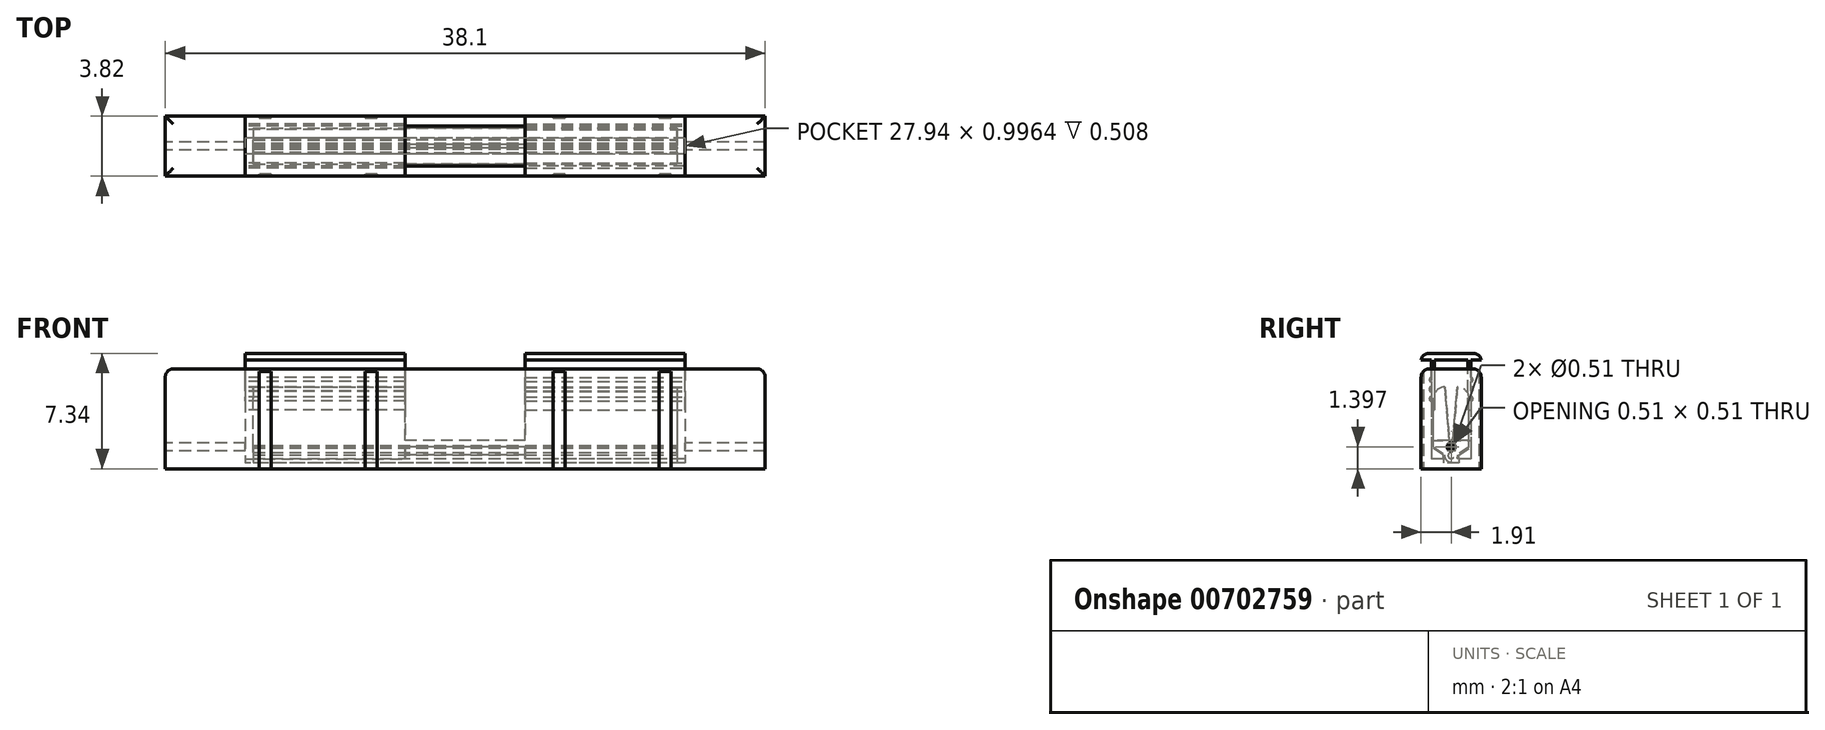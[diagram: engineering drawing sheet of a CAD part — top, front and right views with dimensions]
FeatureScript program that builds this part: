
annotation { "Feature Type Name" : "Feature", "Feature Type Description" : "" }
export const myFeature = defineFeature(function(context is Context, id is Id, definition is map)
    precondition{}
    {
        {
            var Q0;
            Q0=qCreatedBy(makeId("Top.planeOp"),FACE);
            var sketch = newSketch(context, id + "F0", { "sketchPlane" : qUnion([Q0])});
            skLineSegment(sketch, "E0.bottom", {"start": v(19.05, -1.9) * mm, "end": v(-19.05, -1.9) * mm});
            skLineSegment(sketch, "E0.top", {"start": v(19.05, 1.9) * mm, "end": v(-19.05, 1.9) * mm});
            skLineSegment(sketch, "E0.left", {"start": v(19.05, -1.9) * mm, "end": v(19.05, 1.9) * mm});
            skLineSegment(sketch, "E0.right", {"start": v(-19.05, -1.9) * mm, "end": v(-19.05, 1.9) * mm});
            skPoint(sketch, "E0.middle", {"position": v(0, 0) * mm});
            skLineSegment(sketch, "E1", {"start": v(0, 6.77) * mm, "end": v(0, -8.48) * mm, "construction": true});
            skLineSegment(sketch, "E2.bottom", {"start": v(-13.97, 1.27) * mm, "end": v(-3.81, 1.27) * mm});
            skLineSegment(sketch, "E2.top", {"start": v(-13.97, -1.27) * mm, "end": v(-3.81, -1.27) * mm});
            skLineSegment(sketch, "E2.left", {"start": v(-13.97, 1.27) * mm, "end": v(-13.97, -1.27) * mm});
            skLineSegment(sketch, "E2.right", {"start": v(-3.81, 1.27) * mm, "end": v(-3.81, -1.27) * mm});
            skLineSegment(sketch, "E3.MirrorCS", {"start": v(3.81, 1.27) * mm, "end": v(3.81, -1.27) * mm});
            skLineSegment(sketch, "E4.MirrorCS", {"start": v(13.97, 1.27) * mm, "end": v(3.81, 1.27) * mm});
            skLineSegment(sketch, "E5.MirrorCS", {"start": v(13.97, -1.27) * mm, "end": v(3.81, -1.27) * mm});
            skLineSegment(sketch, "E6.MirrorCS", {"start": v(13.97, 1.27) * mm, "end": v(13.97, -1.27) * mm});
            skLineSegment(sketch, "E7", {"start": v(13.08, 1.9) * mm, "end": v(13.08, 1.78) * mm});
            skLineSegment(sketch, "E8", {"start": v(13.08, 1.78) * mm, "end": v(12.32, 1.78) * mm});
            skLineSegment(sketch, "E9", {"start": v(12.32, 1.78) * mm, "end": v(12.32, 1.9) * mm});
            skLineSegment(sketch, "E10", {"start": v(26.93, 0) * mm, "end": v(-31.8, 0) * mm, "construction": true});
            skPoint(sketch, "E10.startSnap0", {"position": v(19.05, 0) * mm});
            skLineSegment(sketch, "E11", {"start": v(6.35, 1.9) * mm, "end": v(6.35, 1.78) * mm});
            skLineSegment(sketch, "E12", {"start": v(6.35, 1.78) * mm, "end": v(5.59, 1.78) * mm});
            skLineSegment(sketch, "E13", {"start": v(5.59, 1.78) * mm, "end": v(5.59, 1.9) * mm});
            skLineSegment(sketch, "E14.MirrorCS", {"start": v(6.35, -1.9) * mm, "end": v(6.35, -1.78) * mm});
            skLineSegment(sketch, "E15.MirrorCS", {"start": v(6.35, -1.78) * mm, "end": v(5.59, -1.78) * mm});
            skLineSegment(sketch, "E16.MirrorCS", {"start": v(5.59, -1.78) * mm, "end": v(5.59, -1.9) * mm});
            skLineSegment(sketch, "E17.MirrorCS", {"start": v(12.32, -1.78) * mm, "end": v(12.32, -1.9) * mm});
            skLineSegment(sketch, "E18.MirrorCS", {"start": v(13.08, -1.78) * mm, "end": v(12.32, -1.78) * mm});
            skLineSegment(sketch, "E19.MirrorCS", {"start": v(13.08, -1.9) * mm, "end": v(13.08, -1.78) * mm});
            skLineSegment(sketch, "E20.MirrorCS", {"start": v(-6.35, 1.78) * mm, "end": v(-5.59, 1.78) * mm});
            skLineSegment(sketch, "E21.MirrorCS", {"start": v(-5.59, 1.78) * mm, "end": v(-5.59, 1.9) * mm});
            skLineSegment(sketch, "E22.MirrorCS", {"start": v(-6.35, 1.9) * mm, "end": v(-6.35, 1.78) * mm});
            skLineSegment(sketch, "E23.MirrorCS", {"start": v(-12.32, 1.78) * mm, "end": v(-12.32, 1.9) * mm});
            skLineSegment(sketch, "E24.MirrorCS", {"start": v(-13.08, 1.78) * mm, "end": v(-12.32, 1.78) * mm});
            skLineSegment(sketch, "E25.MirrorCS", {"start": v(-13.08, 1.9) * mm, "end": v(-13.08, 1.78) * mm});
            skLineSegment(sketch, "E26.MirrorCS", {"start": v(-6.35, -1.9) * mm, "end": v(-6.35, -1.78) * mm});
            skLineSegment(sketch, "E27.MirrorCS", {"start": v(-6.35, -1.78) * mm, "end": v(-5.59, -1.78) * mm});
            skLineSegment(sketch, "E28.MirrorCS", {"start": v(-5.59, -1.78) * mm, "end": v(-5.59, -1.9) * mm});
            skLineSegment(sketch, "E29.MirrorCS", {"start": v(-13.08, -1.9) * mm, "end": v(-13.08, -1.78) * mm});
            skLineSegment(sketch, "E30.MirrorCS", {"start": v(-13.08, -1.78) * mm, "end": v(-12.32, -1.78) * mm});
            skLineSegment(sketch, "E31.MirrorCS", {"start": v(-12.32, -1.78) * mm, "end": v(-12.32, -1.9) * mm});
            skSolve(sketch);
        }
        {
            var Q0;
            Q0=makeQuery(id+"F0.imprint","IMPRINT",FACE,{"disambiguationData":[TD([[makeQuery(id+"F0.imprint","IMPRINT",EDGE,{"derivedFrom":sQuery(id+"F0.wireOp",EDGE,"E0.top")}),1.0]])]});
            extrude(context, id + "F1", {"entities" : qUnion([Q0]), "depth" : 6.35 * mm, "offsetDistance" : 25.4 * mm});
        }
        {
            var Q0;
            Q0=makeQuery(id+"F0.imprint","IMPRINT",FACE,{"disambiguationData":[TD([[makeQuery(id+"F0.imprint","IMPRINT",EDGE,{"derivedFrom":sQuery(id+"F0.wireOp",EDGE,"E2.bottom")}),-1.0]])]});
            var Q1;
            Q1=makeQuery(id+"F0.imprint","IMPRINT",FACE,{"disambiguationData":[TD([[makeQuery(id+"F0.imprint","IMPRINT",EDGE,{"derivedFrom":sQuery(id+"F0.wireOp",EDGE,"E3.MirrorCS")}),1.0]])]});
            extrude(context, id + "F2", {"entities" : qUnion([Q0, Q1]), "operationType" : NewBodyOperationType.ADD, "depth" : 0.64 * mm, "offsetDistance" : 25.4 * mm});
        }
        {
            var Q0;
            Q0=makeQuery(id+"F1.opExtrude","SWEPT_FACE",FACE,{"disambiguationData":[OSD([sQuery(id+"F0.wireOp",EDGE,"E2.left")])]});
            var sketch = newSketch(context, id + "F3", { "sketchPlane" : qUnion([Q0])});
            skLineSegment(sketch, "E32.bottom", {"start": v(0.5, 0.38) * mm, "end": v(-0.5, 0.38) * mm});
            skLineSegment(sketch, "E32.top", {"start": v(1.27, 5.46) * mm, "end": v(-1.27, 5.46) * mm});
            skLineSegment(sketch, "E32.left", {"start": v(1.27, 1.4) * mm, "end": v(1.27, 5.46) * mm});
            skLineSegment(sketch, "E32.right", {"start": v(-1.27, 1.4) * mm, "end": v(-1.27, 5.46) * mm});
            skLineSegment(sketch, "E33", {"start": v(0, 0) * mm, "end": v(0, 8.58) * mm, "construction": true});
            skPoint(sketch, "E34", {"position": v(0, 0.99) * mm});
            skLineSegment(sketch, "E35", {"start": v(0.5, 0.89) * mm, "end": v(0.5, 0.38) * mm});
            skLineSegment(sketch, "E36.MirrorCS", {"start": v(-0.5, 0.89) * mm, "end": v(-0.5, 0.38) * mm});
            skPoint(sketch, "E37.orphan", {"position": v(-0.5, 0.38) * mm});
            skPoint(sketch, "E38.orphan", {"position": v(1.27, 0.38) * mm});
            skLineSegment(sketch, "E39", {"start": v(1.27, 1.4) * mm, "end": v(0.5, 0.89) * mm});
            skLineSegment(sketch, "E40.MirrorCS", {"start": v(-1.27, 1.4) * mm, "end": v(-0.5, 0.89) * mm});
            skSolve(sketch);
        }
        {
            var Q0;
            Q0=qSketchRegion(id+"F3",true);
            var Q1;
            Q1=makeQuery(id+"F1.opExtrude","SWEPT_FACE",FACE,{"disambiguationData":[OSD([sQuery(id+"F0.wireOp",EDGE,"E6.MirrorCS")])]});
            extrude(context, id + "F4", {"entities" : qUnion([Q0]), "operationType" : NewBodyOperationType.REMOVE, "endBound" : BoundingType.UP_TO_SURFACE, "depth" : 10.4 * mm, "endBoundEntityFace" : qUnion([Q1]), "offsetDistance" : 25.4 * mm});
        }
        {
            var Q0;
            Q0=qCreatedBy(makeId("Right.planeOp"),FACE);
            var sketch = newSketch(context, id + "F5", { "sketchPlane" : qUnion([Q0])});
            skCircle(sketch, "E41", {"center": v(0, 1.4) * mm, "radius": 0.1 * mm});
            skLineSegment(sketch, "E42.bottom", {"start": v(1.02, 5.08) * mm, "end": v(-1.02, 5.08) * mm});
            skLineSegment(sketch, "E42.top", {"start": v(1.02, 0) * mm, "end": v(-1.02, 0) * mm});
            skLineSegment(sketch, "E42.left", {"start": v(1.02, 5.08) * mm, "end": v(1.02, 0) * mm});
            skLineSegment(sketch, "E42.right", {"start": v(-1.02, 5.08) * mm, "end": v(-1.02, 0) * mm});
            skLineSegment(sketch, "E43", {"start": v(0, -1.4) * mm, "end": v(0, 7.34) * mm, "construction": true});
            skSolve(sketch);
        }
        {
            var Q0;
            Q0=makeQuery(id+"F1.opExtrude","SWEPT_FACE",FACE,{"disambiguationData":[OSD([sQuery(id+"F0.wireOp",EDGE,"E0.right")])]});
            var sketch = newSketch(context, id + "F6", { "sketchPlane" : qUnion([Q0])});
            skCircle(sketch, "E44", {"center": v(0, 1.4) * mm, "radius": 0.25 * mm});
            skSolve(sketch);
        }
        {
            var Q0;
            Q0=qSketchRegion(id+"F6",true);
            extrude(context, id + "F7", {"entities" : qUnion([Q0]), "operationType" : NewBodyOperationType.REMOVE, "endBound" : BoundingType.THROUGH_ALL, "oppositeDirection" : true, "depth" : 25.4 * mm, "offsetDistance" : 25.4 * mm});
        }
        {
            var Q0;
            Q0=makeQuery(id+"F1.opExtrude","CAP_EDGE",EDGE,{"disambiguationData":[OSD([sQuery(id+"F0.wireOp",EDGE,"E0.right")])],"isStart":false});
            var Q1;
            Q1=makeQuery(id+"F1.opExtrude","CAP_EDGE",EDGE,{"disambiguationData":[OSD([sQuery(id+"F0.wireOp",EDGE,"E0.top")])],"isStart":false});
            var Q2;
            Q2=makeQuery(id+"F1.opExtrude","CAP_EDGE",EDGE,{"disambiguationData":[OSD([sQuery(id+"F0.wireOp",EDGE,"E0.bottom")])],"isStart":false});
            var Q3;
            Q3=makeQuery(id+"F1.opExtrude","CAP_EDGE",EDGE,{"disambiguationData":[OSD([sQuery(id+"F0.wireOp",EDGE,"E0.left")])],"isStart":false});
            fillet(context, id + "F8", {"entities" : qUnion([Q0, Q1, Q2, Q3]), "radius" : 0.5 * mm, "tangentPropagation" : true, "allowEdgeOverflow" : false});
        }
        {
            var Q0;
            Q0=makeQuery(id+"F1.opExtrude","SWEPT_FACE",FACE,{"disambiguationData":[OSD([sQuery(id+"F0.wireOp",EDGE,"E2.right")])]});
            var sketch = newSketch(context, id + "F9", { "sketchPlane" : qUnion([Q0])});
            skLineSegment(sketch, "E45.bottom", {"start": v(-0.38, 5.2) * mm, "end": v(0.38, 5.2) * mm});
            skLineSegment(sketch, "E45.top", {"start": v(-1.14, 0.38) * mm, "end": v(1.14, 0.38) * mm});
            skLineSegment(sketch, "E45.left", {"start": v(-1.14, 4.45) * mm, "end": v(-1.14, 0.38) * mm});
            skLineSegment(sketch, "E45.right", {"start": v(1.14, 4.45) * mm, "end": v(1.14, 0.38) * mm});
            skPoint(sketch, "E46.visualSharp", {"position": v(1.14, 5.2) * mm});
            skArc(sketch, "E46.filletArc", {"start": v(1.14, 4.45) * mm, "mid": v(0.92, 4.98) * mm, "end": v(0.38, 5.2) * mm});
            skPoint(sketch, "E47.visualSharp", {"position": v(-1.14, 5.2) * mm});
            skArc(sketch, "E47.filletArc", {"start": v(-0.38, 5.2) * mm, "mid": v(-0.92, 4.98) * mm, "end": v(-1.14, 4.45) * mm});
            skPoint(sketch, "E48.trimOffspring.end.orphan", {"position": v(0, 0.38) * mm});
            skLineSegment(sketch, "E49", {"start": v(-0.38, 5.2) * mm, "end": v(-0.09, 1.48) * mm});
            skLineSegment(sketch, "E50.MirrorCS", {"start": v(0.38, 5.2) * mm, "end": v(0.09, 1.48) * mm});
            skArc(sketch, "E51", {"start": v(-0.05, 1.03) * mm, "mid": v(0, 0.65) * mm, "end": v(0.05, 1.03) * mm});
            skLineSegment(sketch, "E52.trimOffspring", {"start": v(-0.08, 1.34) * mm, "end": v(-0.05, 1.03) * mm});
            skLineSegment(sketch, "E53.trimOffspring", {"start": v(0.08, 1.34) * mm, "end": v(0.05, 1.03) * mm});
            skArc(sketch, "E54", {"start": v(-0.42, 0.9) * mm, "mid": v(0, 0.42) * mm, "end": v(0.42, 0.9) * mm});
            skLineSegment(sketch, "E55", {"start": v(-0.42, 0.9) * mm, "end": v(-1.14, 1.4) * mm});
            skLineSegment(sketch, "E56.MirrorCS", {"start": v(0.42, 0.9) * mm, "end": v(1.14, 1.4) * mm});
            skArc(sketch, "E57", {"start": v(-0.09, 1.48) * mm, "mid": v(-0.2, 1.4) * mm, "end": v(-0.08, 1.34) * mm});
            skPoint(sketch, "E57.first.point", {"position": v(-0.08, 1.34) * mm});
            skPoint(sketch, "E57.second.point", {"position": v(-0.09, 1.48) * mm});
            skPoint(sketch, "E57.third.point", {"position": v(-0.2, 1.42) * mm});
            skArc(sketch, "E58.MirrorCS", {"start": v(0.08, 1.34) * mm, "mid": v(0.13, 1.4) * mm, "end": v(0.09, 1.48) * mm});
            skPoint(sketch, "E59.MirrorC.end.orphan", {"position": v(0.09, 1.48) * mm});
            skPoint(sketch, "E59.MirrorC.start.orphan", {"position": v(0.08, 1.34) * mm});
            skLineSegment(sketch, "E60.trimOffspring", {"start": v(0.08, 1.34) * mm, "end": v(0.08, 1.34) * mm});
            skLineSegment(sketch, "E61.trimOffspring", {"start": v(-0.08, 1.34) * mm, "end": v(-0.08, 1.34) * mm});
            skSolve(sketch);
        }
        {
            var Q0;
            {var subQ3=sQuery(id+"F9.wireOp",EDGE,"E46.filletArc");Q0=makeQuery(id+"F9.imprint","IMPRINT",FACE,{"disambiguationData":[TD([[makeQuery(id+"F9.imprint","IMPRINT",EDGE,{"derivedFrom":subQ3}),1.0]])]});}
            var Q1;
            Q1=makeQuery(id+"F4.boolean.opBoolean","MERGE",FACE,{"derivedFrom":[makeQuery(id+"F1.opExtrude","SWEPT_FACE",FACE,{"disambiguationData":[OSD([sQuery(id+"F0.wireOp",EDGE,"E2.left")])]}),makeQuery(id+"F4.opExtrude","CAP_FACE",FACE,{"disambiguationData":[OSD([sQuery(id+"F3.wireOp",EDGE,"E32.bottom"),sQuery(id+"F3.wireOp",EDGE,"E32.top"),sQuery(id+"F3.wireOp",EDGE,"E32.left"),sQuery(id+"F3.wireOp",EDGE,"E32.right"),sQuery(id+"F3.wireOp",EDGE,"E35"),sQuery(id+"F3.wireOp",EDGE,"E36.MirrorCS"),sQuery(id+"F3.wireOp",EDGE,"E39"),sQuery(id+"F3.wireOp",EDGE,"E40.MirrorCS")])],"isStart":true})]});
            extrude(context, id + "F10", {"entities" : qUnion([Q0]), "endBound" : BoundingType.UP_TO_SURFACE, "depth" : 7.62 * mm, "endBoundEntityFace" : qUnion([Q1]), "hasOffset" : true, "offsetDistance" : 0.5 * mm});
        }
        {
            var Q0;
            Q0=makeQuery(id+"F10.opExtrude","CAP_FACE",FACE,{"disambiguationData":[OSD([sQuery(id+"F9.wireOp",EDGE,"E45.left"),sQuery(id+"F9.wireOp",EDGE,"E45.right"),sQuery(id+"F9.wireOp",EDGE,"E46.filletArc"),sQuery(id+"F9.wireOp",EDGE,"E47.filletArc"),sQuery(id+"F9.wireOp",EDGE,"E50.MirrorCS"),sQuery(id+"F9.wireOp",EDGE,"E51"),sQuery(id+"F9.wireOp",EDGE,"E52.trimOffspring"),sQuery(id+"F9.wireOp",EDGE,"E53.trimOffspring"),sQuery(id+"F9.wireOp",EDGE,"E54"),sQuery(id+"F9.wireOp",EDGE,"E55"),sQuery(id+"F9.wireOp",EDGE,"E56.MirrorCS"),sQuery(id+"F9.wireOp",EDGE,"E57"),sQuery(id+"F9.wireOp",EDGE,"E49"),sQuery(id+"F9.wireOp",EDGE,"E58.MirrorCS"),sQuery(id+"F9.wireOp",EDGE,"E60.trimOffspring"),sQuery(id+"F9.wireOp",EDGE,"E61.trimOffspring")])],"isStart":true});
            var Q1;
            {var subQ0=sQuery(id+"F0.wireOp",EDGE,"E6.MirrorCS");Q1=makeQuery(id+"F4.boolean.opBoolean","MERGE",FACE,{"derivedFrom":[makeQuery(id+"F1.opExtrude","SWEPT_FACE",FACE,{"disambiguationData":[OSD([subQ0])]}),makeQuery(id+"F4.opExtrude","CAP_FACE",FACE,{"disambiguationData":[OSD([subQ0])],"isStart":false})]});}
            extrude(context, id + "F11", {"entities" : qUnion([Q0]), "operationType" : NewBodyOperationType.ADD, "endBound" : BoundingType.UP_TO_SURFACE, "depth" : 25.4 * mm, "endBoundEntityFace" : qUnion([Q1]), "hasOffset" : true, "offsetDistance" : 0.5 * mm});
        }
        {
            var Q0;
            Q0=qCreatedBy(makeId("Right.planeOp"),FACE);
            var sketch = newSketch(context, id + "F12", { "sketchPlane" : qUnion([Q0])});
            skLineSegment(sketch, "E62.bottom", {"start": v(1.26, 5.32) * mm, "end": v(-1.26, 5.32) * mm});
            skLineSegment(sketch, "E62.top", {"start": v(1.26, 1.8) * mm, "end": v(-1.26, 1.8) * mm});
            skLineSegment(sketch, "E62.left", {"start": v(1.26, 5.32) * mm, "end": v(1.26, 1.8) * mm});
            skLineSegment(sketch, "E62.right", {"start": v(-1.26, 5.32) * mm, "end": v(-1.26, 1.8) * mm});
            skSolve(sketch);
        }
        {
            var Q0;
            Q0=qSketchRegion(id+"F12",true);
            extrude(context, id + "F13", {"entities" : qUnion([Q0]), "operationType" : NewBodyOperationType.REMOVE, "endBound" : BoundingType.SYMMETRIC, "oppositeDirection" : true, "depth" : 7.62 * mm, "offsetDistance" : 25.4 * mm});
        }
        {
            var Q0;
            Q0=makeQuery(id+"F4.boolean.opBoolean","COPY",FACE,{"derivedFrom":makeQuery(id+"F4.opExtrude","SWEPT_FACE",FACE,{"disambiguationData":[OSD([sQuery(id+"F3.wireOp",EDGE,"E32.top")])]})});
            extrude(context, id + "F14", {"entities" : qUnion([Q0]), "operationType" : NewBodyOperationType.ADD, "depth" : 3.3 * mm, "offsetDistance" : 25.4 * mm});
        }
        {
            var Q0;
            Q0=makeQuery(id+"F4.boolean.opBoolean","MERGE",FACE,{"derivedFrom":[makeQuery(id+"F1.opExtrude","SWEPT_FACE",FACE,{"disambiguationData":[OSD([sQuery(id+"F0.wireOp",EDGE,"E2.left")])]}),makeQuery(id+"F4.opExtrude","CAP_FACE",FACE,{"disambiguationData":[OSD([sQuery(id+"F3.wireOp",EDGE,"E32.bottom"),sQuery(id+"F3.wireOp",EDGE,"E32.top"),sQuery(id+"F3.wireOp",EDGE,"E32.left"),sQuery(id+"F3.wireOp",EDGE,"E32.right"),sQuery(id+"F3.wireOp",EDGE,"E35"),sQuery(id+"F3.wireOp",EDGE,"E36.MirrorCS"),sQuery(id+"F3.wireOp",EDGE,"E39"),sQuery(id+"F3.wireOp",EDGE,"E40.MirrorCS")])],"isStart":true})]});
            var sketch = newSketch(context, id + "F15", { "sketchPlane" : qUnion([Q0])});
            skLineSegment(sketch, "E63.left", {"start": v(1.27, 4.32) * mm, "end": v(1.27, 4.57) * mm});
            skLineSegment(sketch, "E63.right", {"start": v(-1.27, 4.32) * mm, "end": v(-1.27, 4.57) * mm});
            skArc(sketch, "E64", {"start": v(-1.27, 5.2) * mm, "mid": v(-1.4, 5.08) * mm, "end": v(-1.27, 4.95) * mm});
            skArc(sketch, "E65", {"start": v(-1.27, 4.57) * mm, "mid": v(-1.4, 4.44) * mm, "end": v(-1.27, 4.32) * mm});
            skArc(sketch, "E66.MirrorC", {"start": v(1.27, 5.2) * mm, "mid": v(1.4, 5.08) * mm, "end": v(1.27, 4.95) * mm});
            skArc(sketch, "E67.MirrorC", {"start": v(1.27, 4.57) * mm, "mid": v(1.4, 4.45) * mm, "end": v(1.27, 4.32) * mm});
            skLineSegment(sketch, "E68.trimOffspring", {"start": v(-1.27, 4.95) * mm, "end": v(-1.27, 5.2) * mm});
            skLineSegment(sketch, "E69.trimOffspring", {"start": v(1.27, 4.95) * mm, "end": v(1.27, 5.2) * mm});
            skSolve(sketch);
        }
        {
            var Q0;
            Q0=qSketchRegion(id+"F15",true);
            var Q1;
            {var subQ0=sQuery(id+"F3.wireOp",EDGE,"E32.top");var subQ1=sQuery(id+"F0.wireOp",EDGE,"E2.right");Q1=makeQuery(id+"F14.boolean.opBoolean","MERGE",FACE,{"derivedFrom":[makeQuery(id+"F4.boolean.opBoolean","SPLIT",FACE,{"disambiguationData":[TD([makeQuery(id+"F4.opExtrude","SWEPT_FACE",FACE,{"disambiguationData":[OSD([subQ0])]})])],"derivedFrom":makeQuery(id+"F1.opExtrude","SWEPT_FACE",FACE,{"disambiguationData":[OSD([subQ1])]})}),makeQuery(id+"F14.opExtrude","SWEPT_FACE",FACE,{"disambiguationData":[OSD([subQ1,subQ0])]})]});}
            extrude(context, id + "F16", {"entities" : qUnion([Q0]), "operationType" : NewBodyOperationType.REMOVE, "endBound" : BoundingType.UP_TO_SURFACE, "depth" : 25.4 * mm, "endBoundEntityFace" : qUnion([Q1]), "offsetDistance" : 25.4 * mm});
        }
        {
            var Q0;
            {var subQ0=sQuery(id+"F0.wireOp",EDGE,"E6.MirrorCS");Q0=makeQuery(id+"F4.boolean.opBoolean","MERGE",FACE,{"derivedFrom":[makeQuery(id+"F1.opExtrude","SWEPT_FACE",FACE,{"disambiguationData":[OSD([subQ0])]}),makeQuery(id+"F4.opExtrude","CAP_FACE",FACE,{"disambiguationData":[OSD([subQ0])],"isStart":false})]});}
            var sketch = newSketch(context, id + "F17", { "sketchPlane" : qUnion([Q0])});
            skLineSegment(sketch, "E70.left", {"start": v(1.27, 4.32) * mm, "end": v(1.27, 4.57) * mm});
            skLineSegment(sketch, "E70.right", {"start": v(-1.27, 4.32) * mm, "end": v(-1.27, 4.57) * mm});
            skArc(sketch, "E71", {"start": v(-1.27, 5.2) * mm, "mid": v(-1.4, 5.08) * mm, "end": v(-1.27, 4.95) * mm});
            skArc(sketch, "E72", {"start": v(-1.27, 4.57) * mm, "mid": v(-1.4, 4.45) * mm, "end": v(-1.27, 4.32) * mm});
            skArc(sketch, "E73.MirrorC", {"start": v(1.27, 5.2) * mm, "mid": v(1.4, 5.08) * mm, "end": v(1.27, 4.95) * mm});
            skArc(sketch, "E74.MirrorC", {"start": v(1.27, 4.57) * mm, "mid": v(1.4, 4.45) * mm, "end": v(1.27, 4.32) * mm});
            skLineSegment(sketch, "E75.trimOffspring", {"start": v(-1.27, 4.95) * mm, "end": v(-1.27, 5.2) * mm});
            skLineSegment(sketch, "E76.trimOffspring", {"start": v(1.27, 4.95) * mm, "end": v(1.27, 5.2) * mm});
            skSolve(sketch);
        }
        {
            var Q0;
            Q0=qSketchRegion(id+"F17",true);
            var Q1;
            {var subQ0=sQuery(id+"F3.wireOp",EDGE,"E32.top");var subQ1=sQuery(id+"F0.wireOp",EDGE,"E3.MirrorCS");Q1=makeQuery(id+"F14.boolean.opBoolean","MERGE",FACE,{"derivedFrom":[makeQuery(id+"F4.boolean.opBoolean","SPLIT",FACE,{"disambiguationData":[TD([makeQuery(id+"F4.opExtrude","SWEPT_FACE",FACE,{"disambiguationData":[OSD([subQ0])]})])],"derivedFrom":makeQuery(id+"F1.opExtrude","SWEPT_FACE",FACE,{"disambiguationData":[OSD([subQ1])]})}),makeQuery(id+"F14.opExtrude","SWEPT_FACE",FACE,{"disambiguationData":[OSD([subQ1,subQ0])]})]});}
            extrude(context, id + "F18", {"entities" : qUnion([Q0]), "operationType" : NewBodyOperationType.REMOVE, "endBound" : BoundingType.UP_TO_SURFACE, "depth" : 25.4 * mm, "endBoundEntityFace" : qUnion([Q1]), "offsetDistance" : 25.4 * mm});
        }
        {
            var Q0;
            {var subQ0=sQuery(id+"F0.wireOp",EDGE,"E6.MirrorCS");Q0=makeQuery(id+"F18.boolean.opBoolean","MERGE",FACE,{"derivedFrom":[makeQuery(id+"F4.boolean.opBoolean","MERGE",FACE,{"derivedFrom":[makeQuery(id+"F1.opExtrude","SWEPT_FACE",FACE,{"disambiguationData":[OSD([subQ0])]}),makeQuery(id+"F4.opExtrude","CAP_FACE",FACE,{"disambiguationData":[OSD([subQ0])],"isStart":false})]}),makeQuery(id+"F18.opExtrude","CAP_FACE",FACE,{"disambiguationData":[OSD([sQuery(id+"F17.wireOp",EDGE,"E70.left"),sQuery(id+"F17.wireOp",EDGE,"E74.MirrorC")])],"isStart":true}),makeQuery(id+"F18.opExtrude","CAP_FACE",FACE,{"disambiguationData":[OSD([sQuery(id+"F17.wireOp",EDGE,"E70.right"),sQuery(id+"F17.wireOp",EDGE,"E72")])],"isStart":true}),makeQuery(id+"F18.opExtrude","CAP_FACE",FACE,{"disambiguationData":[OSD([sQuery(id+"F17.wireOp",EDGE,"E71"),sQuery(id+"F17.wireOp",EDGE,"E75.trimOffspring")])],"isStart":true}),makeQuery(id+"F18.opExtrude","CAP_FACE",FACE,{"disambiguationData":[OSD([sQuery(id+"F17.wireOp",EDGE,"E73.MirrorC"),sQuery(id+"F17.wireOp",EDGE,"E76.trimOffspring")])],"isStart":true})]});}
            var sketch = newSketch(context, id + "F19", { "sketchPlane" : qUnion([Q0])});
            skLineSegment(sketch, "E77.bottom", {"start": v(-1.27, 3.74) * mm, "end": v(-1.07, 3.74) * mm});
            skLineSegment(sketch, "E77.top", {"start": v(-1.07, 6.92) * mm, "end": v(1.07, 6.92) * mm});
            skLineSegment(sketch, "E77.left", {"start": v(-1.27, 3.74) * mm, "end": v(-1.27, 4.9) * mm});
            skLineSegment(sketch, "E77.right", {"start": v(1.27, 3.74) * mm, "end": v(1.27, 4.9) * mm});
            skLineSegment(sketch, "E78.bottom", {"start": v(-1.9, 7.34) * mm, "end": v(1.9, 7.34) * mm});
            skLineSegment(sketch, "E78.top", {"start": v(-1.9, 6.92) * mm, "end": v(-1.27, 6.92) * mm});
            skLineSegment(sketch, "E78.left", {"start": v(-1.9, 7.34) * mm, "end": v(-1.9, 6.92) * mm});
            skLineSegment(sketch, "E78.right", {"start": v(1.9, 7.34) * mm, "end": v(1.9, 6.92) * mm});
            skLineSegment(sketch, "E79.0", {"start": v(-1.07, 3.94) * mm, "end": v(-1.07, 6.92) * mm});
            skLineSegment(sketch, "E79.2", {"start": v(1.07, 4.4) * mm, "end": v(1.07, 6.92) * mm});
            skLineSegment(sketch, "E80", {"start": v(-1.07, 3.94) * mm, "end": v(-1.07, 3.74) * mm});
            skLineSegment(sketch, "E81", {"start": v(1.07, 4.4) * mm, "end": v(1.07, 3.74) * mm});
            skLineSegment(sketch, "E82.trimOffspring", {"start": v(1.07, 3.74) * mm, "end": v(1.27, 3.74) * mm});
            skLineSegment(sketch, "E83.trimOffspring", {"start": v(1.27, 6.92) * mm, "end": v(1.9, 6.92) * mm});
            skArc(sketch, "E84", {"start": v(1.27, 5.54) * mm, "mid": v(1.4, 5.67) * mm, "end": v(1.27, 5.8) * mm});
            skPoint(sketch, "E84.centerSnap0", {"position": v(1.07, 5.67) * mm});
            skArc(sketch, "E85", {"start": v(1.27, 4.9) * mm, "mid": v(1.4, 5.03) * mm, "end": v(1.27, 5.16) * mm});
            skLineSegment(sketch, "E86", {"start": v(0, 6.92) * mm, "end": v(0, 3.1) * mm, "construction": true});
            skArc(sketch, "E87.MirrorCS", {"start": v(-1.27, 5.54) * mm, "mid": v(-1.4, 5.67) * mm, "end": v(-1.27, 5.8) * mm});
            skArc(sketch, "E88.MirrorCS", {"start": v(-1.27, 4.9) * mm, "mid": v(-1.4, 5.03) * mm, "end": v(-1.27, 5.16) * mm});
            skLineSegment(sketch, "E89.trimOffspring", {"start": v(-1.27, 5.8) * mm, "end": v(-1.27, 6.92) * mm});
            skLineSegment(sketch, "E90.trimOffspring", {"start": v(-1.27, 5.16) * mm, "end": v(-1.27, 5.54) * mm});
            skLineSegment(sketch, "E91.trimOffspring", {"start": v(1.27, 5.16) * mm, "end": v(1.27, 5.54) * mm});
            skLineSegment(sketch, "E92.trimOffspring", {"start": v(1.27, 5.8) * mm, "end": v(1.27, 6.92) * mm});
            skSolve(sketch);
        }
        {
            var Q0;
            Q0=qSketchRegion(id+"F19",true);
            var Q1;
            {var subQ0=sQuery(id+"F3.wireOp",EDGE,"E32.top");var subQ1=sQuery(id+"F0.wireOp",EDGE,"E3.MirrorCS");Q1=makeQuery(id+"F18.boolean.opBoolean","MERGE",FACE,{"derivedFrom":[makeQuery(id+"F14.boolean.opBoolean","MERGE",FACE,{"derivedFrom":[makeQuery(id+"F4.boolean.opBoolean","SPLIT",FACE,{"disambiguationData":[TD([makeQuery(id+"F4.opExtrude","SWEPT_FACE",FACE,{"disambiguationData":[OSD([subQ0])]})])],"derivedFrom":makeQuery(id+"F1.opExtrude","SWEPT_FACE",FACE,{"disambiguationData":[OSD([subQ1])]})}),makeQuery(id+"F14.opExtrude","SWEPT_FACE",FACE,{"disambiguationData":[OSD([subQ1,subQ0])]})]}),makeQuery(id+"F18.opExtrude","CAP_FACE",FACE,{"disambiguationData":[OSD([sQuery(id+"F17.wireOp",EDGE,"E70.left"),sQuery(id+"F17.wireOp",EDGE,"E74.MirrorC")])],"isStart":false}),makeQuery(id+"F18.opExtrude","CAP_FACE",FACE,{"disambiguationData":[OSD([sQuery(id+"F17.wireOp",EDGE,"E70.right"),sQuery(id+"F17.wireOp",EDGE,"E72")])],"isStart":false}),makeQuery(id+"F18.opExtrude","CAP_FACE",FACE,{"disambiguationData":[OSD([sQuery(id+"F17.wireOp",EDGE,"E71"),sQuery(id+"F17.wireOp",EDGE,"E75.trimOffspring")])],"isStart":false}),makeQuery(id+"F18.opExtrude","CAP_FACE",FACE,{"disambiguationData":[OSD([sQuery(id+"F17.wireOp",EDGE,"E73.MirrorC"),sQuery(id+"F17.wireOp",EDGE,"E76.trimOffspring")])],"isStart":false})]});}
            extrude(context, id + "F20", {"entities" : qUnion([Q0]), "endBound" : BoundingType.UP_TO_SURFACE, "depth" : 25.4 * mm, "endBoundEntityFace" : qUnion([Q1]), "offsetDistance" : 25.4 * mm});
        }
        {
            var Q0;
            Q0=makeQuery(id+"F20.opExtrude","SWEPT_EDGE",EDGE,{"disambiguationData":[OSD([sQuery(id+"F19.wireOp",EDGE,"E78.bottom"),sQuery(id+"F19.wireOp",EDGE,"E78.left")])]});
            var Q1;
            Q1=makeQuery(id+"F20.opExtrude","SWEPT_EDGE",EDGE,{"disambiguationData":[OSD([sQuery(id+"F19.wireOp",EDGE,"E78.bottom"),sQuery(id+"F19.wireOp",EDGE,"E78.right")])]});
            fillet(context, id + "F21", {"entities" : qUnion([Q0, Q1]), "radius" : 0.5 * mm, "tangentPropagation" : true, "allowEdgeOverflow" : false});
        }
        {
            var Q0;
            Q0=makeQuery(id+"F3.imprint","IMPRINT",FACE,{"disambiguationData":[TD([[makeQuery(id+"F3.imprint","IMPRINT",EDGE,{"derivedFrom":sQuery(id+"F3.wireOp",EDGE,"E32.top")}),1.0]])]});
            var sketch = newSketch(context, id + "F22", { "sketchPlane" : qUnion([Q0])});
            skLineSegment(sketch, "E93.bottom", {"start": v(-1.27, 3.74) * mm, "end": v(-1.07, 3.74) * mm});
            skLineSegment(sketch, "E93.top", {"start": v(-1.07, 6.92) * mm, "end": v(1.07, 6.92) * mm});
            skLineSegment(sketch, "E93.left", {"start": v(-1.27, 3.74) * mm, "end": v(-1.27, 4.9) * mm});
            skLineSegment(sketch, "E93.right", {"start": v(1.27, 3.74) * mm, "end": v(1.27, 4.9) * mm});
            skLineSegment(sketch, "E94.bottom", {"start": v(-1.9, 7.34) * mm, "end": v(1.9, 7.34) * mm});
            skLineSegment(sketch, "E94.top", {"start": v(-1.9, 6.92) * mm, "end": v(-1.27, 6.92) * mm});
            skLineSegment(sketch, "E94.left", {"start": v(-1.9, 7.34) * mm, "end": v(-1.9, 6.92) * mm});
            skLineSegment(sketch, "E94.right", {"start": v(1.9, 7.34) * mm, "end": v(1.9, 6.92) * mm});
            skLineSegment(sketch, "E95.0", {"start": v(-1.07, 3.94) * mm, "end": v(-1.07, 6.92) * mm});
            skLineSegment(sketch, "E95.2", {"start": v(1.07, 4.4) * mm, "end": v(1.07, 6.92) * mm});
            skLineSegment(sketch, "E96", {"start": v(-1.07, 3.94) * mm, "end": v(-1.07, 3.74) * mm});
            skLineSegment(sketch, "E97", {"start": v(1.07, 4.4) * mm, "end": v(1.07, 3.74) * mm});
            skLineSegment(sketch, "E98.trimOffspring", {"start": v(1.07, 3.74) * mm, "end": v(1.27, 3.74) * mm});
            skLineSegment(sketch, "E99.trimOffspring", {"start": v(1.27, 6.92) * mm, "end": v(1.9, 6.92) * mm});
            skArc(sketch, "E100", {"start": v(1.27, 5.54) * mm, "mid": v(1.4, 5.67) * mm, "end": v(1.27, 5.8) * mm});
            skPoint(sketch, "E100.centerSnap0", {"position": v(1.07, 5.67) * mm});
            skArc(sketch, "E101", {"start": v(1.27, 4.9) * mm, "mid": v(1.4, 5.03) * mm, "end": v(1.27, 5.16) * mm});
            skLineSegment(sketch, "E102", {"start": v(0, 6.92) * mm, "end": v(0, 3.1) * mm, "construction": true});
            skArc(sketch, "E103.MirrorCS", {"start": v(-1.27, 5.54) * mm, "mid": v(-1.4, 5.67) * mm, "end": v(-1.27, 5.8) * mm});
            skArc(sketch, "E104.MirrorCS", {"start": v(-1.27, 4.9) * mm, "mid": v(-1.4, 5.03) * mm, "end": v(-1.27, 5.16) * mm});
            skLineSegment(sketch, "E105.trimOffspring", {"start": v(-1.27, 5.8) * mm, "end": v(-1.27, 6.92) * mm});
            skLineSegment(sketch, "E106.trimOffspring", {"start": v(-1.27, 5.16) * mm, "end": v(-1.27, 5.54) * mm});
            skLineSegment(sketch, "E107.trimOffspring", {"start": v(1.27, 5.16) * mm, "end": v(1.27, 5.54) * mm});
            skLineSegment(sketch, "E108.trimOffspring", {"start": v(1.27, 5.8) * mm, "end": v(1.27, 6.92) * mm});
            skSolve(sketch);
        }
        {
            var Q0;
            Q0=qSketchRegion(id+"F22",true);
            var Q1;
            {var subQ0=sQuery(id+"F3.wireOp",EDGE,"E32.top");var subQ1=sQuery(id+"F0.wireOp",EDGE,"E2.right");Q1=makeQuery(id+"F16.boolean.opBoolean","MERGE",FACE,{"derivedFrom":[makeQuery(id+"F14.boolean.opBoolean","MERGE",FACE,{"derivedFrom":[makeQuery(id+"F4.boolean.opBoolean","SPLIT",FACE,{"disambiguationData":[TD([makeQuery(id+"F4.opExtrude","SWEPT_FACE",FACE,{"disambiguationData":[OSD([subQ0])]})])],"derivedFrom":makeQuery(id+"F1.opExtrude","SWEPT_FACE",FACE,{"disambiguationData":[OSD([subQ1])]})}),makeQuery(id+"F14.opExtrude","SWEPT_FACE",FACE,{"disambiguationData":[OSD([subQ1,subQ0])]})]}),makeQuery(id+"F16.opExtrude","CAP_FACE",FACE,{"disambiguationData":[OSD([sQuery(id+"F15.wireOp",EDGE,"E63.left"),sQuery(id+"F15.wireOp",EDGE,"E67.MirrorC")])],"isStart":false}),makeQuery(id+"F16.opExtrude","CAP_FACE",FACE,{"disambiguationData":[OSD([sQuery(id+"F15.wireOp",EDGE,"E63.right"),sQuery(id+"F15.wireOp",EDGE,"E65")])],"isStart":false}),makeQuery(id+"F16.opExtrude","CAP_FACE",FACE,{"disambiguationData":[OSD([sQuery(id+"F15.wireOp",EDGE,"E64"),sQuery(id+"F15.wireOp",EDGE,"E68.trimOffspring")])],"isStart":false}),makeQuery(id+"F16.opExtrude","CAP_FACE",FACE,{"disambiguationData":[OSD([sQuery(id+"F15.wireOp",EDGE,"E66.MirrorC"),sQuery(id+"F15.wireOp",EDGE,"E69.trimOffspring")])],"isStart":false})]});}
            extrude(context, id + "F23", {"entities" : qUnion([Q0]), "endBound" : BoundingType.UP_TO_SURFACE, "depth" : 25.4 * mm, "endBoundEntityFace" : qUnion([Q1]), "offsetDistance" : 25.4 * mm});
        }
        {
            var Q0;
            Q0=makeQuery(id+"F23.opExtrude","SWEPT_EDGE",EDGE,{"disambiguationData":[OSD([sQuery(id+"F22.wireOp",EDGE,"E94.bottom"),sQuery(id+"F22.wireOp",EDGE,"E94.left")])]});
            var Q1;
            Q1=makeQuery(id+"F23.opExtrude","SWEPT_EDGE",EDGE,{"disambiguationData":[OSD([sQuery(id+"F22.wireOp",EDGE,"E94.bottom"),sQuery(id+"F22.wireOp",EDGE,"E94.right")])]});
            fillet(context, id + "F24", {"entities" : qUnion([Q0, Q1]), "radius" : 0.5 * mm, "tangentPropagation" : true, "allowEdgeOverflow" : false});
        }
        {
            var Q0;
            Q0=makeQuery(id+"F1.opExtrude","CAP_FACE",FACE,{"disambiguationData":[OSD([sQuery(id+"F0.wireOp",EDGE,"E0.bottom"),sQuery(id+"F0.wireOp",EDGE,"E0.top"),sQuery(id+"F0.wireOp",EDGE,"E0.left"),sQuery(id+"F0.wireOp",EDGE,"E0.right"),sQuery(id+"F0.wireOp",EDGE,"E2.bottom"),sQuery(id+"F0.wireOp",EDGE,"E2.top"),sQuery(id+"F0.wireOp",EDGE,"E2.left"),sQuery(id+"F0.wireOp",EDGE,"E2.right"),sQuery(id+"F0.wireOp",EDGE,"E3.MirrorCS"),sQuery(id+"F0.wireOp",EDGE,"E4.MirrorCS"),sQuery(id+"F0.wireOp",EDGE,"E5.MirrorCS"),sQuery(id+"F0.wireOp",EDGE,"E6.MirrorCS")])],"isStart":false});
            var sketch = newSketch(context, id + "F25", { "sketchPlane" : qUnion([Q0])});
            skLineSegment(sketch, "E109.bottom", {"start": v(-3.81, 1.27) * mm, "end": v(3.81, 1.27) * mm});
            skLineSegment(sketch, "E109.top", {"start": v(-3.81, -1.27) * mm, "end": v(3.81, -1.27) * mm});
            skLineSegment(sketch, "E109.left", {"start": v(-3.81, 1.27) * mm, "end": v(-3.81, -1.27) * mm});
            skLineSegment(sketch, "E109.right", {"start": v(3.81, 1.27) * mm, "end": v(3.81, -1.27) * mm});
            skSolve(sketch);
        }
        {
            var Q0;
            Q0=makeQuery(id+"F25.imprint","IMPRINT",FACE,{"disambiguationData":[TD([[makeQuery(id+"F25.imprint","IMPRINT",EDGE,{"derivedFrom":sQuery(id+"F25.wireOp",EDGE,"E109.bottom")}),-1.0]])]});
            var Q1;
            {var subQ0=sQuery(id+"F9.wireOp",EDGE,"E45.left");var subQ4=sQuery(id+"F12.wireOp",EDGE,"E62.top");Q1=makeQuery(id+"F13.boolean.opBoolean","COPY",FACE,{"disambiguationData":[TD([makeQuery(id+"F10.opExtrude","SWEPT_FACE",FACE,{"disambiguationData":[OSD([subQ0])]})])],"derivedFrom":makeQuery(id+"F13.opExtrude","SWEPT_FACE",FACE,{"disambiguationData":[OSD([subQ4])]})});}
            extrude(context, id + "F26", {"entities" : qUnion([Q0]), "operationType" : NewBodyOperationType.REMOVE, "endBound" : BoundingType.UP_TO_SURFACE, "oppositeDirection" : true, "depth" : 25.4 * mm, "endBoundEntityFace" : qUnion([Q1]), "offsetDistance" : 25.4 * mm});
        }
        {
            var Q0;
            {var subQ0=sQuery(id+"F9.wireOp",EDGE,"E45.left");var subQ4=sQuery(id+"F12.wireOp",EDGE,"E62.top");Q0=makeQuery(id+"F13.boolean.opBoolean","COPY",FACE,{"disambiguationData":[TD([makeQuery(id+"F10.opExtrude","SWEPT_FACE",FACE,{"disambiguationData":[OSD([subQ0])]})])],"derivedFrom":makeQuery(id+"F13.opExtrude","SWEPT_FACE",FACE,{"disambiguationData":[OSD([subQ4])]})});}
            var sketch = newSketch(context, id + "F27", { "sketchPlane" : qUnion([Q0])});
            skLineSegment(sketch, "E110.bottom", {"start": v(3.81, -1.27) * mm, "end": v(-3.81, -1.27) * mm});
            skLineSegment(sketch, "E110.top", {"start": v(3.81, 1.27) * mm, "end": v(-3.81, 1.27) * mm});
            skLineSegment(sketch, "E110.left", {"start": v(3.81, -1.27) * mm, "end": v(3.81, 1.27) * mm});
            skLineSegment(sketch, "E110.right", {"start": v(-3.81, -1.27) * mm, "end": v(-3.81, 1.27) * mm});
            skPoint(sketch, "E110.middle", {"position": v(0, 0) * mm});
            skSolve(sketch);
        }
        {
            var Q0;
            Q0=qSketchRegion(id+"F27",true);
            var Q1;
            Q1=makeQuery(id+"F1.opExtrude","CAP_FACE",FACE,{"disambiguationData":[OSD([sQuery(id+"F0.wireOp",EDGE,"E0.bottom"),sQuery(id+"F0.wireOp",EDGE,"E0.top"),sQuery(id+"F0.wireOp",EDGE,"E0.left"),sQuery(id+"F0.wireOp",EDGE,"E0.right"),sQuery(id+"F0.wireOp",EDGE,"E2.bottom"),sQuery(id+"F0.wireOp",EDGE,"E2.top"),sQuery(id+"F0.wireOp",EDGE,"E2.left"),sQuery(id+"F0.wireOp",EDGE,"E2.right"),sQuery(id+"F0.wireOp",EDGE,"E3.MirrorCS"),sQuery(id+"F0.wireOp",EDGE,"E4.MirrorCS"),sQuery(id+"F0.wireOp",EDGE,"E5.MirrorCS"),sQuery(id+"F0.wireOp",EDGE,"E6.MirrorCS")])],"isStart":false});
            var Q2;
            {var subQ1=sQuery(id+"F9.wireOp",EDGE,"E45.right");var subQ4=sQuery(id+"F12.wireOp",EDGE,"E62.top");Q2=makeQuery(id+"F13.boolean.opBoolean","COPY",FACE,{"disambiguationData":[TD([makeQuery(id+"F10.opExtrude","SWEPT_FACE",FACE,{"disambiguationData":[OSD([subQ1])]})])],"derivedFrom":makeQuery(id+"F13.opExtrude","SWEPT_FACE",FACE,{"disambiguationData":[OSD([subQ4])]})});}
            extrude(context, id + "F28", {"entities" : qUnion([Q0]), "endBound" : BoundingType.UP_TO_SURFACE, "depth" : 25.4 * mm, "endBoundEntityFace" : qUnion([Q1]), "offsetDistance" : 2.54 * mm});
        }
    });
